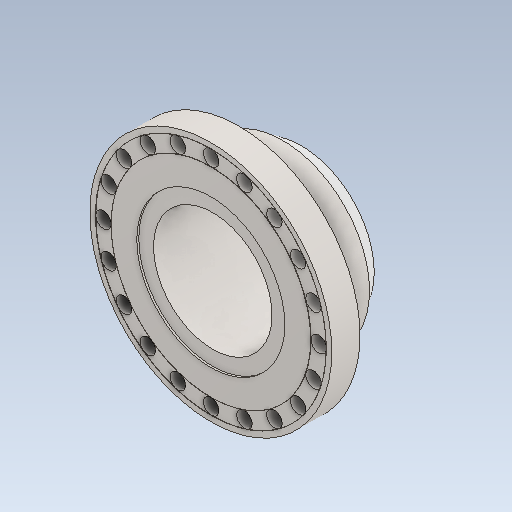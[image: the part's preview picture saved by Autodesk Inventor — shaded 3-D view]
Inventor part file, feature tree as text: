
AUTODESK INVENTOR PART (.ipt)
format: ipt  version: 2021 (Build 250183000, 183)  size: 242,688 bytes
history: mixed  units: in
note: dims shown in document units (in); Inventor stores cm internally (conversion verified against a paired STEP export)
features: chamfer x1, imported_body x1
ambient origin geometry x8: Origin, YZ Plane, XZ Plane, XY Plane, X Axis, Y Axis, Z Axis, Center Point
bodies: Solid1 (imported_parasolid)
feature tree (2):
  chamfer  "Chamfer2"  [1 undecoded]
  imported_body  NMx_Import_Brep_tag  [imported B-rep: ~54 faces, bbox_mm=[892.234217, 871.229213, 341.33028]]
note: 1 required parameter value undecoded (feature->parameter linkage not recoverable at this tier; creation-order binding heuristic only, values carry confidence <= 0.55)
